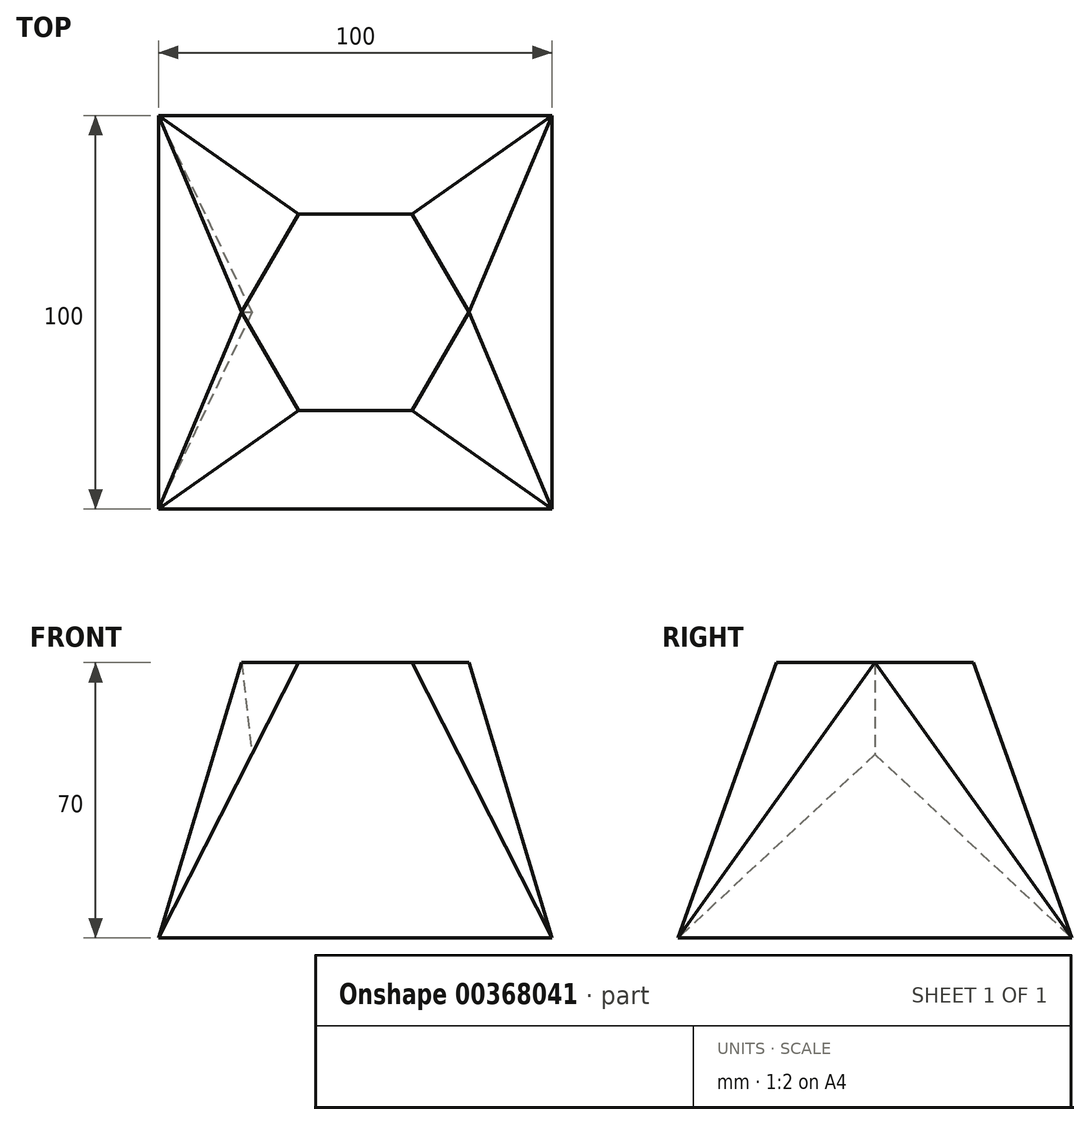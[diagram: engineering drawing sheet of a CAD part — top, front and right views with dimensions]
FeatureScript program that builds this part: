
annotation { "Feature Type Name" : "Feature", "Feature Type Description" : "" }
export const myFeature = defineFeature(function(context is Context, id is Id, definition is map)
    precondition{}
    {
        {
            var Q0;
            Q0=qCreatedBy(makeId("Top.planeOp"),FACE);
            var sketch = newSketch(context, id + "F0", { "sketchPlane" : qUnion([Q0])});
            skLineSegment(sketch, "E0.bottom", {"start": v(50, -50) * mm, "end": v(-50, -50) * mm});
            skLineSegment(sketch, "E0.top", {"start": v(50, 50) * mm, "end": v(-50, 50) * mm});
            skLineSegment(sketch, "E0.left", {"start": v(50, -50) * mm, "end": v(50, 50) * mm});
            skLineSegment(sketch, "E0.right", {"start": v(-50, -50) * mm, "end": v(-50, 50) * mm});
            skPoint(sketch, "E0.middle", {"position": v(0, 0) * mm});
            skSolve(sketch);
        }
        {
            var Q0;
            Q0=qCreatedBy(makeId("Top.planeOp"),FACE);
            cPlane(context, id + "F1", {"entities" : qUnion([Q0]), "cplaneType" : CPlaneType.OFFSET, "offset" : 70 * mm, "width" : 150 * mm, "height" : 150 * mm});
        }
        {
            var Q0;
            Q0=qCreatedBy(id+"F1.planeOp",FACE);
            var sketch = newSketch(context, id + "F2", { "sketchPlane" : qUnion([Q0])});
            skCircle(sketch, "E1.cCircle", {"center": v(0, 0) * mm, "radius": 25 * mm, "construction": true});
            skLineSegment(sketch, "E1.0", {"start": v(-14.43, 25) * mm, "end": v(14.43, 25) * mm});
            skLineSegment(sketch, "E1.1", {"start": v(14.43, 25) * mm, "end": v(28.87, 0) * mm});
            skLineSegment(sketch, "E1.2", {"start": v(28.87, 0) * mm, "end": v(14.43, -25) * mm});
            skLineSegment(sketch, "E1.3", {"start": v(14.43, -25) * mm, "end": v(-14.43, -25) * mm});
            skLineSegment(sketch, "E1.4", {"start": v(-14.43, -25) * mm, "end": v(-28.87, 0) * mm});
            skLineSegment(sketch, "E1.5", {"start": v(-28.87, 0) * mm, "end": v(-14.43, 25) * mm});
            skPoint(sketch, "E1.0.midPoint", {"position": v(0, 25) * mm});
            skLineSegment(sketch, "E2", {"start": v(-14.43, 25) * mm, "end": v(-14.43, -25) * mm});
            skLineSegment(sketch, "E3", {"start": v(14.43, 25) * mm, "end": v(14.43, -25) * mm});
            skSolve(sketch);
        }
        {
            var Q0;
            Q0=makeQuery(id+"F0.imprint","IMPRINT",FACE,{"disambiguationData":[TD([[makeQuery(id+"F0.imprint","IMPRINT",EDGE,{"derivedFrom":sQuery(id+"F0.wireOp",EDGE,"E0.bottom")}),-1.0]])]});
            var Q1;
            Q1=makeQuery(id+"F2.imprint","IMPRINT",FACE,{"disambiguationData":[TD([[makeQuery(id+"F2.imprint","IMPRINT",EDGE,{"derivedFrom":sQuery(id+"F2.wireOp",EDGE,"E1.0")}),-1.0]])]});
            loft(context, id + "F3", {"sheetProfilesArray" : [{ "sheetProfileEntities" : qUnion([Q0]) }, { "sheetProfileEntities" : qUnion([Q1]) }]});
        }
        {
            var Q1;
            Q1=makeQuery(id+"F2.imprint","IMPRINT",FACE,{"disambiguationData":[TD([[makeQuery(id+"F2.imprint","IMPRINT",EDGE,{"derivedFrom":sQuery(id+"F2.wireOp",EDGE,"E1.1")}),-1.0]])]});
            var Q2;
            Q2=makeQuery(id+"F3.opLoft","MID_CAP_VERTEX",VERTEX,{"disambiguationData":[OSD([sQuery(id+"F0.wireOp",EDGE,"E0.bottom"),sQuery(id+"F0.wireOp",EDGE,"E0.left")])],"capPos":0.0});
            loft(context, id + "F4", {"operationType" : NewBodyOperationType.ADD, "sheetProfilesArray" : [{ "sheetProfileEntities" : qUnion([Q1]) }, { "sheetProfileEntities" : qUnion([Q2]) }]});
        }
        {
            var Q1;
            Q1=makeQuery(id+"F2.imprint","IMPRINT",FACE,{"disambiguationData":[TD([[makeQuery(id+"F2.imprint","IMPRINT",EDGE,{"derivedFrom":sQuery(id+"F2.wireOp",EDGE,"E1.1")}),-1.0]])]});
            var Q2;
            Q2=makeQuery(id+"F3.opLoft","MID_CAP_VERTEX",VERTEX,{"disambiguationData":[OSD([sQuery(id+"F0.wireOp",EDGE,"E0.top"),sQuery(id+"F0.wireOp",EDGE,"E0.left")])],"capPos":0.0});
            loft(context, id + "F5", {"operationType" : NewBodyOperationType.ADD, "sheetProfilesArray" : [{ "sheetProfileEntities" : qUnion([Q1]) }, { "sheetProfileEntities" : qUnion([Q2]) }]});
        }
        {
            var Q1;
            Q1=makeQuery(id+"F5.opLoft","SWEPT_FACE",FACE,{"disambiguationData":[OSD([sQuery(id+"F2.wireOp",EDGE,"E1.1"),sQuery(id+"F2.wireOp",EDGE,"E1.2"),sQuery(id+"F2.wireOp",EDGE,"E1.3"),sQuery(id+"F2.wireOp",EDGE,"E3")])]});
            var Q2;
            Q2=makeQuery(id+"F4.opLoft","SWEPT_FACE",FACE,{"disambiguationData":[OSD([sQuery(id+"F2.wireOp",EDGE,"E1.0"),sQuery(id+"F2.wireOp",EDGE,"E1.1"),sQuery(id+"F2.wireOp",EDGE,"E1.2"),sQuery(id+"F2.wireOp",EDGE,"E3")])]});
            var Q3;
            {var subQ0=sQuery(id+"F0.wireOp",EDGE,"E0.left");var subQ1=sQuery(id+"F0.wireOp",EDGE,"E0.top");Q3=makeQuery(id+"F5.boolean.opBoolean","MERGE",VERTEX,{"derivedFrom":[makeQuery(id+"F3.opLoft","MID_CAP_VERTEX",VERTEX,{"disambiguationData":[OSD([subQ1,subQ0])],"capPos":0.0}),makeQuery(id+"F5.opLoft","SWEPT_VERTEX",VERTEX,{"disambiguationData":[OSD([subQ1,subQ0,sQuery(id+"F2.wireOp",EDGE,"E1.1"),sQuery(id+"F2.wireOp",EDGE,"E1.2")])]})]});}
            var Q4;
            {var subQ0=sQuery(id+"F0.wireOp",EDGE,"E0.left");var subQ1=sQuery(id+"F0.wireOp",EDGE,"E0.bottom");Q4=makeQuery(id+"F4.boolean.opBoolean","MERGE",VERTEX,{"derivedFrom":[makeQuery(id+"F3.opLoft","MID_CAP_VERTEX",VERTEX,{"disambiguationData":[OSD([subQ1,subQ0])],"capPos":0.0}),makeQuery(id+"F4.opLoft","SWEPT_VERTEX",VERTEX,{"disambiguationData":[OSD([subQ1,subQ0,sQuery(id+"F2.wireOp",EDGE,"E1.1"),sQuery(id+"F2.wireOp",EDGE,"E1.2")])]})]});}
            loft(context, id + "F6", {"operationType" : NewBodyOperationType.ADD, "sheetProfilesArray" : [{ "sheetProfileEntities" : qUnion([Q1]) }, { "sheetProfileEntities" : qUnion([Q2]) }], "matchConnections" : true, "connections" : [{ "connectionEntities" : qUnion([Q3, Q4]), "connectionEdgeQueries" : qUnion([]), "connectionEdgeParameters" : [] }]});
        }
        {
            var Q1;
            Q1=makeQuery(id+"F2.imprint","IMPRINT",FACE,{"disambiguationData":[TD([[makeQuery(id+"F2.imprint","IMPRINT",EDGE,{"derivedFrom":sQuery(id+"F2.wireOp",EDGE,"E1.4")}),-1.0]])]});
            var Q2;
            Q2=makeQuery(id+"F3.opLoft","MID_CAP_VERTEX",VERTEX,{"disambiguationData":[OSD([sQuery(id+"F0.wireOp",EDGE,"E0.top"),sQuery(id+"F0.wireOp",EDGE,"E0.right")])],"capPos":0.0});
            loft(context, id + "F7", {"operationType" : NewBodyOperationType.ADD, "sheetProfilesArray" : [{ "sheetProfileEntities" : qUnion([Q1]) }, { "sheetProfileEntities" : qUnion([Q2]) }]});
        }
        {
            var Q1;
            Q1=makeQuery(id+"F2.imprint","IMPRINT",FACE,{"disambiguationData":[TD([[makeQuery(id+"F2.imprint","IMPRINT",EDGE,{"derivedFrom":sQuery(id+"F2.wireOp",EDGE,"E1.4")}),-1.0]])]});
            var Q2;
            Q2=makeQuery(id+"F3.opLoft","MID_CAP_VERTEX",VERTEX,{"disambiguationData":[OSD([sQuery(id+"F0.wireOp",EDGE,"E0.bottom"),sQuery(id+"F0.wireOp",EDGE,"E0.right")])],"capPos":0.0});
            loft(context, id + "F8", {"operationType" : NewBodyOperationType.ADD, "sheetProfilesArray" : [{ "sheetProfileEntities" : qUnion([Q1]) }, { "sheetProfileEntities" : qUnion([Q2]) }]});
        }
        {
            var Q1;
            Q1=makeQuery(id+"F8.opLoft","SWEPT_FACE",FACE,{"disambiguationData":[OSD([sQuery(id+"F2.wireOp",EDGE,"E1.0"),sQuery(id+"F2.wireOp",EDGE,"E1.4"),sQuery(id+"F2.wireOp",EDGE,"E1.5"),sQuery(id+"F2.wireOp",EDGE,"E2")])]});
            var Q2;
            Q2=makeQuery(id+"F7.opLoft","SWEPT_FACE",FACE,{"disambiguationData":[OSD([sQuery(id+"F2.wireOp",EDGE,"E1.3"),sQuery(id+"F2.wireOp",EDGE,"E1.4"),sQuery(id+"F2.wireOp",EDGE,"E1.5"),sQuery(id+"F2.wireOp",EDGE,"E2")])]});
            var Q3;
            {var subQ0=sQuery(id+"F0.wireOp",EDGE,"E0.right");var subQ1=sQuery(id+"F0.wireOp",EDGE,"E0.bottom");Q3=makeQuery(id+"F8.boolean.opBoolean","MERGE",VERTEX,{"derivedFrom":[makeQuery(id+"F3.opLoft","MID_CAP_VERTEX",VERTEX,{"disambiguationData":[OSD([subQ1,subQ0])],"capPos":0.0}),makeQuery(id+"F8.opLoft","SWEPT_VERTEX",VERTEX,{"disambiguationData":[OSD([subQ1,subQ0,sQuery(id+"F2.wireOp",EDGE,"E1.3"),sQuery(id+"F2.wireOp",EDGE,"E1.4"),sQuery(id+"F2.wireOp",EDGE,"E2")])]})]});}
            var Q4;
            {var subQ0=sQuery(id+"F0.wireOp",EDGE,"E0.right");var subQ1=sQuery(id+"F0.wireOp",EDGE,"E0.top");Q4=makeQuery(id+"F7.boolean.opBoolean","MERGE",VERTEX,{"derivedFrom":[makeQuery(id+"F3.opLoft","MID_CAP_VERTEX",VERTEX,{"disambiguationData":[OSD([subQ1,subQ0])],"capPos":0.0}),makeQuery(id+"F7.opLoft","SWEPT_VERTEX",VERTEX,{"disambiguationData":[OSD([subQ1,subQ0,sQuery(id+"F2.wireOp",EDGE,"E1.3"),sQuery(id+"F2.wireOp",EDGE,"E1.4"),sQuery(id+"F2.wireOp",EDGE,"E2")])]})]});}
            loft(context, id + "F9", {"sheetProfilesArray" : [{ "sheetProfileEntities" : qUnion([Q1]) }, { "sheetProfileEntities" : qUnion([Q2]) }], "matchConnections" : true, "connections" : [{ "connectionEntities" : qUnion([Q3, Q4]), "connectionEdgeQueries" : qUnion([]), "connectionEdgeParameters" : [] }]});
        }
    });
